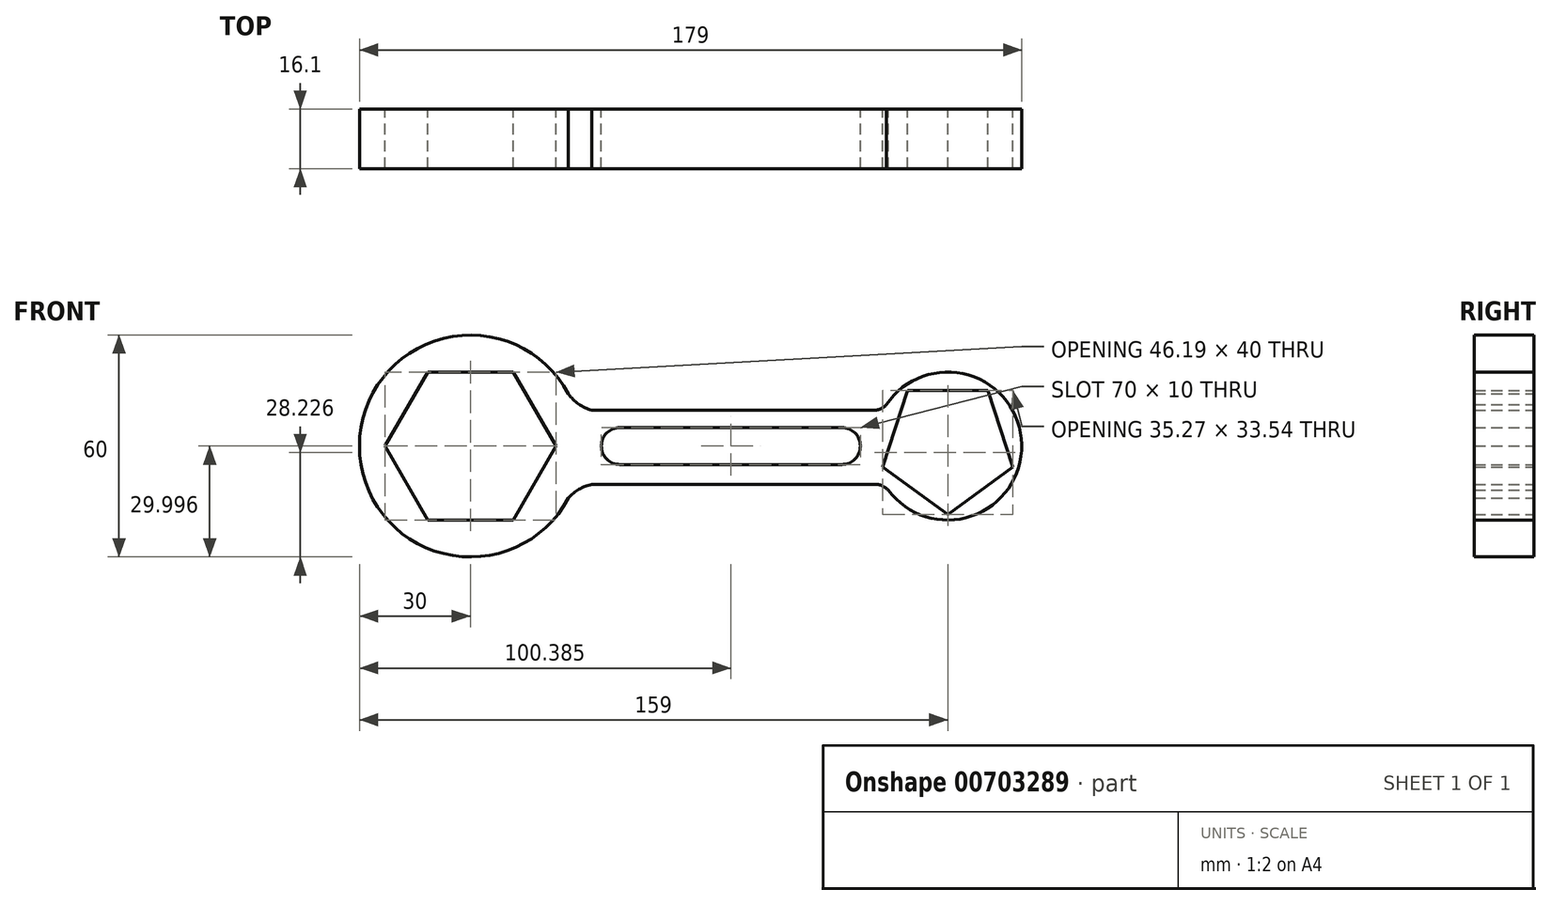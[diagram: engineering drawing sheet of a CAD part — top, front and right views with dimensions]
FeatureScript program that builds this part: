
annotation { "Feature Type Name" : "Feature", "Feature Type Description" : "" }
export const myFeature = defineFeature(function(context is Context, id is Id, definition is map)
    precondition{}
    {
        {
            var Q0;
            Q0=qCreatedBy(makeId("Front.planeOp"),FACE);
            var sketch = newSketch(context, id + "F0", { "sketchPlane" : qUnion([Q0])});
            skCircle(sketch, "E0", {"center": v(-129, 7.74) * mm, "radius": 30 * mm});
            skCircle(sketch, "E1", {"center": v(0, 7.74) * mm, "radius": 20 * mm});
            skArc(sketch, "E2", {"start": v(-88.61, 12.74) * mm, "mid": v(-93.61, 7.74) * mm, "end": v(-88.61, 2.74) * mm});
            skArc(sketch, "E3", {"start": v(-28.61, 2.74) * mm, "mid": v(-23.61, 7.74) * mm, "end": v(-28.61, 12.74) * mm});
            skLineSegment(sketch, "E4", {"start": v(-88.61, 12.74) * mm, "end": v(-28.61, 12.74) * mm});
            skLineSegment(sketch, "E5", {"start": v(-28.61, 2.74) * mm, "end": v(-88.61, 2.74) * mm});
            skLineSegment(sketch, "E6", {"start": v(-96.19, 17.4) * mm, "end": v(-19.96, 17.4) * mm});
            skLineSegment(sketch, "E7", {"start": v(-96.19, -2.6) * mm, "end": v(-19.8, -2.6) * mm});
            skArc(sketch, "E8", {"start": v(-102.5, 21.8) * mm, "mid": v(-99.73, 19.05) * mm, "end": v(-96.19, 17.4) * mm});
            skArc(sketch, "E9", {"start": v(-96.19, -2.6) * mm, "mid": v(-99.65, -3.96) * mm, "end": v(-102.5, -6.34) * mm});
            skPoint(sketch, "E10.orphan", {"position": v(-22.38, 17.4) * mm});
            skPoint(sketch, "E11.orphan", {"position": v(-22.38, -2.6) * mm});
            skArc(sketch, "E12", {"start": v(-19.96, 17.4) * mm, "mid": v(-17.71, 18) * mm, "end": v(-16.07, 19.64) * mm});
            skArc(sketch, "E13", {"start": v(-16.07, -4.17) * mm, "mid": v(-17.77, -3.01) * mm, "end": v(-19.8, -2.6) * mm});
            skCircle(sketch, "E14.cCircle", {"center": v(-129, 7.74) * mm, "radius": 20 * mm, "construction": true});
            skLineSegment(sketch, "E14.0", {"start": v(-140.55, 27.74) * mm, "end": v(-117.45, 27.74) * mm});
            skLineSegment(sketch, "E14.1", {"start": v(-117.45, 27.74) * mm, "end": v(-105.9, 7.74) * mm});
            skLineSegment(sketch, "E14.2", {"start": v(-105.9, 7.74) * mm, "end": v(-117.45, -12.26) * mm});
            skLineSegment(sketch, "E14.3", {"start": v(-117.45, -12.26) * mm, "end": v(-140.55, -12.26) * mm});
            skLineSegment(sketch, "E14.4", {"start": v(-140.55, -12.26) * mm, "end": v(-152.1, 7.74) * mm});
            skLineSegment(sketch, "E14.5", {"start": v(-152.1, 7.74) * mm, "end": v(-140.55, 27.74) * mm});
            skPoint(sketch, "E14.0.midPoint", {"position": v(-129, 27.74) * mm});
            skCircle(sketch, "E15.cCircle", {"center": v(0, 7.74) * mm, "radius": 15 * mm, "construction": true});
            skLineSegment(sketch, "E15.0", {"start": v(-10.9, 22.74) * mm, "end": v(10.9, 22.74) * mm});
            skLineSegment(sketch, "E15.1", {"start": v(10.9, 22.74) * mm, "end": v(17.63, 2) * mm});
            skLineSegment(sketch, "E15.2", {"start": v(17.63, 2) * mm, "end": v(0, -10.8) * mm});
            skLineSegment(sketch, "E15.3", {"start": v(0, -10.8) * mm, "end": v(-17.63, 2) * mm});
            skLineSegment(sketch, "E15.4", {"start": v(-17.63, 2) * mm, "end": v(-10.9, 22.74) * mm});
            skPoint(sketch, "E15.0.midPoint", {"position": v(0, 22.74) * mm});
            skSolve(sketch);
        }
        {
            var Q0;
            Q0 = qSketchRegion(id + "F0", true);
            extrude(context, id + "F1", {"entities" : qUnion([Q0]), "depth" : 16.1 * mm, "offsetDistance" : 25 * mm});
        }
    });
